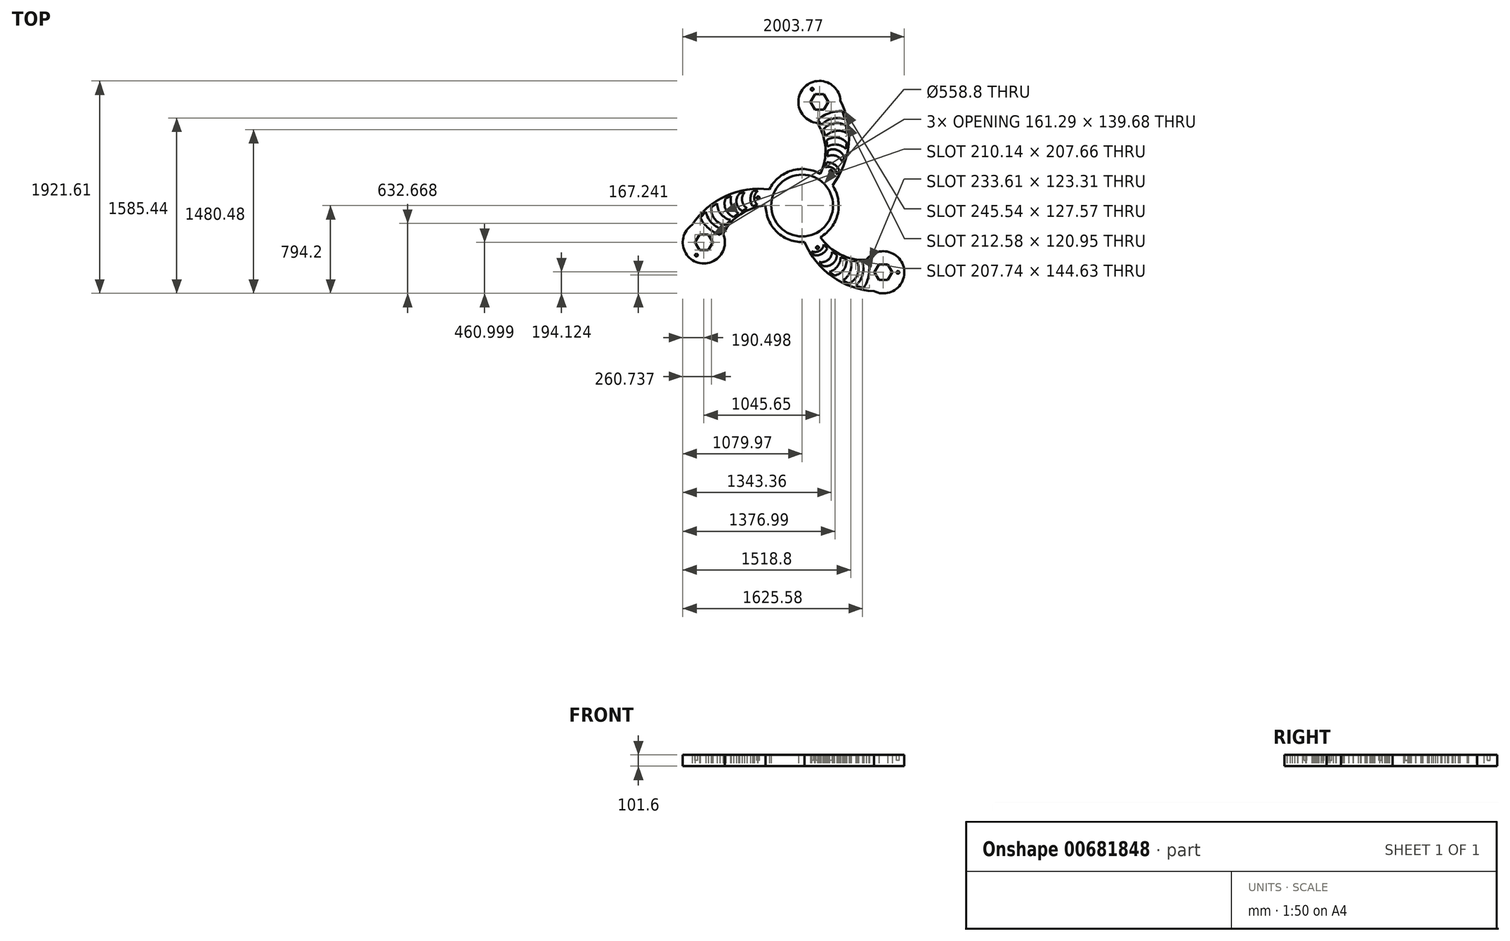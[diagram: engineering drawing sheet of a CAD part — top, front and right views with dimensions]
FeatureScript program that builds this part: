
annotation { "Feature Type Name" : "Feature", "Feature Type Description" : "" }
export const myFeature = defineFeature(function(context is Context, id is Id, definition is map)
    precondition{}
    {
        {
            var Q0;
            Q0=qCreatedBy(makeId("Top.planeOp"),FACE);
            var sketch = newSketch(context, id + "F0", { "sketchPlane" : qUnion([Q0])});
            skCircle(sketch, "E0", {"center": v(0, 0) * mm, "radius": 330.2 * mm});
            skArc(sketch, "E1", {"start": v(-295.98, 146.38) * mm, "mid": v(-691.32, 85.79) * mm, "end": v(-994.94, -174.56) * mm});
            skArc(sketch, "E2", {"start": v(-330.2, 0) * mm, "mid": v(-555.62, -78.09) * mm, "end": v(-715.84, -254.83) * mm});
            skArc(sketch, "E3", {"start": v(-818.87, -156.27) * mm, "mid": v(-998.12, -489.68) * mm, "end": v(-748.36, -205.22) * mm});
            skArc(sketch, "E4", {"start": v(-444.2, 130.87) * mm, "mid": v(-467.95, 63.66) * mm, "end": v(-447.52, -4.64) * mm});
            skLineSegment(sketch, "E5", {"start": v(-447.52, -4.64) * mm, "end": v(-403.07, 7.83) * mm});
            skLineSegment(sketch, "E6", {"start": v(-444.2, 130.87) * mm, "end": v(-399.74, 133.02) * mm});
            skArc(sketch, "E7", {"start": v(-399.74, 133.02) * mm, "mid": v(-432.98, 71.27) * mm, "end": v(-403.07, 7.83) * mm});
            skPoint(sketch, "E8.end.orphan", {"position": v(-453.15, 0) * mm});
            skLineSegment(sketch, "E9", {"start": v(-544.04, -48.42) * mm, "end": v(-498.32, -24.6) * mm});
            skLineSegment(sketch, "E10", {"start": v(-566.11, 110.29) * mm, "end": v(-520.4, 120.58) * mm});
            skArc(sketch, "E11", {"start": v(-520.4, 120.58) * mm, "mid": v(-542.84, 42.9) * mm, "end": v(-498.32, -24.6) * mm});
            skLineSegment(sketch, "E12", {"start": v(-620.12, -103.4) * mm, "end": v(-576.11, -68.97) * mm});
            skLineSegment(sketch, "E13", {"start": v(-693.63, 63.67) * mm, "end": v(-642.31, 85.79) * mm});
            skPoint(sketch, "E13.endSnap0", {"position": v(-691.32, 85.79) * mm});
            skArc(sketch, "E14", {"start": v(-693.63, 63.67) * mm, "mid": v(-690.53, -34.67) * mm, "end": v(-620.12, -103.4) * mm});
            skArc(sketch, "E15", {"start": v(-566.11, 110.29) * mm, "mid": v(-593.67, 25.57) * mm, "end": v(-544.04, -48.42) * mm});
            skArc(sketch, "E16", {"start": v(-642.31, 85.79) * mm, "mid": v(-634.72, -2.5) * mm, "end": v(-576.11, -68.97) * mm});
            skLineSegment(sketch, "E17", {"start": v(-821.71, -15.36) * mm, "end": v(-769.83, 21.24) * mm});
            skLineSegment(sketch, "E18", {"start": v(-689.25, -177.7) * mm, "end": v(-647.8, -129.6) * mm});
            skArc(sketch, "E19", {"start": v(-821.71, -15.36) * mm, "mid": v(-788.75, -123.68) * mm, "end": v(-689.25, -177.7) * mm});
            skArc(sketch, "E20", {"start": v(-769.83, 21.24) * mm, "mid": v(-735.26, -75.57) * mm, "end": v(-647.8, -129.6) * mm});
            skCircle(sketch, "E21.cCircle", {"center": v(-889.47, -333.2) * mm, "radius": 80.65 * mm, "construction": true});
            skLineSegment(sketch, "E21.0", {"start": v(-808.83, -333.2) * mm, "end": v(-849.15, -403.04) * mm});
            skLineSegment(sketch, "E21.1", {"start": v(-849.15, -403.04) * mm, "end": v(-929.8, -403.04) * mm});
            skLineSegment(sketch, "E21.2", {"start": v(-929.8, -403.04) * mm, "end": v(-970.12, -333.2) * mm});
            skLineSegment(sketch, "E21.3", {"start": v(-970.12, -333.2) * mm, "end": v(-929.8, -263.36) * mm});
            skLineSegment(sketch, "E21.4", {"start": v(-929.8, -263.36) * mm, "end": v(-849.15, -263.36) * mm});
            skLineSegment(sketch, "E21.5", {"start": v(-849.15, -263.36) * mm, "end": v(-808.83, -333.2) * mm});
            skLineSegment(sketch, "E22", {"start": v(-870.12, -56.46) * mm, "end": v(-923.06, -111.26) * mm});
            skLineSegment(sketch, "E23", {"start": v(-715.4, -215.8) * mm, "end": v(-743, -266.6) * mm});
            skArc(sketch, "E24", {"start": v(-870.12, -56.46) * mm, "mid": v(-816.29, -158.98) * mm, "end": v(-715.4, -215.8) * mm});
            skArc(sketch, "E25", {"start": v(-923.06, -111.26) * mm, "mid": v(-847.1, -205.24) * mm, "end": v(-743, -266.6) * mm});
            skArc(sketch, "E26.1.0", {"start": v(165.1, -285.96) * mm, "mid": v(345.43, -442.13) * mm, "end": v(578.6, -492.52) * mm});
            skArc(sketch, "E26.1.1", {"start": v(21.22, -329.52) * mm, "mid": v(271.37, -641.6) * mm, "end": v(648.64, -774.36) * mm});
            skArc(sketch, "E26.2.0", {"start": v(165.1, 285.96) * mm, "mid": v(210.18, 520.22) * mm, "end": v(137.23, 747.35) * mm});
            skArc(sketch, "E26.2.1", {"start": v(274.76, 183.14) * mm, "mid": v(419.96, 555.8) * mm, "end": v(346.3, 948.92) * mm});
            skLineSegment(sketch, "E27.1.0", {"start": v(813.94, -603.7) * mm, "end": v(773.62, -673.55) * mm});
            skLineSegment(sketch, "E27.1.1", {"start": v(692.97, -673.55) * mm, "end": v(652.65, -603.7) * mm});
            skLineSegment(sketch, "E27.1.2", {"start": v(773.62, -673.55) * mm, "end": v(692.97, -673.55) * mm});
            skLineSegment(sketch, "E27.2.0", {"start": v(115.85, 1006.75) * mm, "end": v(196.5, 1006.75) * mm});
            skLineSegment(sketch, "E27.2.1", {"start": v(236.82, 936.9) * mm, "end": v(196.5, 867.07) * mm});
            skLineSegment(sketch, "E27.2.2", {"start": v(196.5, 1006.75) * mm, "end": v(236.82, 936.9) * mm});
            skLineSegment(sketch, "E28.1.0", {"start": v(187.54, -545.4) * mm, "end": v(155.77, -510.96) * mm});
            skLineSegment(sketch, "E28.1.2", {"start": v(291.67, -632.53) * mm, "end": v(246.86, -599.15) * mm});
            skLineSegment(sketch, "E28.1.3", {"start": v(424.16, -703.94) * mm, "end": v(366.51, -677.31) * mm});
            skArc(sketch, "E28.1.4", {"start": v(544.77, -631.03) * mm, "mid": v(923.14, -619.56) * mm, "end": v(551.9, -545.49) * mm});
            skCircle(sketch, "E28.1.5", {"center": v(733.3, -603.7) * mm, "radius": 80.65 * mm, "construction": true});
            skLineSegment(sketch, "E28.1.6", {"start": v(399.62, -485.34) * mm, "end": v(347.8, -464.44) * mm});
            skArc(sketch, "E28.1.8", {"start": v(246.86, -599.15) * mm, "mid": v(319.53, -548.43) * mm, "end": v(347.8, -464.44) * mm});
            skLineSegment(sketch, "E28.1.10", {"start": v(483.96, -725.31) * mm, "end": v(557.89, -743.76) * mm});
            skArc(sketch, "E28.1.11", {"start": v(155.77, -510.96) * mm, "mid": v(234.26, -491.56) * mm, "end": v(270.46, -419.26) * mm});
            skLineSegment(sketch, "E28.1.12", {"start": v(108.76, -450.11) * mm, "end": v(84.67, -412.7) * mm});
            skArc(sketch, "E28.1.13", {"start": v(291.67, -632.53) * mm, "mid": v(375.3, -580.68) * mm, "end": v(399.62, -485.34) * mm});
            skArc(sketch, "E28.1.15", {"start": v(424.16, -703.94) * mm, "mid": v(501.48, -621.24) * mm, "end": v(498.52, -508.06) * mm});
            skArc(sketch, "E28.1.16", {"start": v(366.51, -677.31) * mm, "mid": v(433.08, -598.97) * mm, "end": v(436.13, -496.2) * mm});
            skLineSegment(sketch, "E28.1.17", {"start": v(227.78, -385.24) * mm, "end": v(194.75, -352.98) * mm});
            skArc(sketch, "E28.1.18", {"start": v(108.76, -450.11) * mm, "mid": v(178.85, -437.09) * mm, "end": v(227.78, -385.24) * mm});
            skArc(sketch, "E28.1.19", {"start": v(557.89, -743.76) * mm, "mid": v(601.29, -630.99) * mm, "end": v(602.38, -510.16) * mm});
            skLineSegment(sketch, "E28.1.20", {"start": v(773.62, -533.86) * mm, "end": v(813.94, -603.7) * mm});
            skLineSegment(sketch, "E28.1.21", {"start": v(498.52, -508.06) * mm, "end": v(436.13, -496.2) * mm});
            skArc(sketch, "E28.1.23", {"start": v(84.67, -412.7) * mm, "mid": v(154.77, -410.6) * mm, "end": v(194.75, -352.98) * mm});
            skLineSegment(sketch, "E28.1.24", {"start": v(313.95, -446.94) * mm, "end": v(270.46, -419.26) * mm});
            skArc(sketch, "E28.1.25", {"start": v(187.54, -545.4) * mm, "mid": v(274.7, -526.92) * mm, "end": v(313.95, -446.94) * mm});
            skLineSegment(sketch, "E28.1.26", {"start": v(544.6, -511.66) * mm, "end": v(602.38, -510.16) * mm});
            skLineSegment(sketch, "E28.1.27", {"start": v(652.65, -603.7) * mm, "end": v(692.97, -533.86) * mm});
            skLineSegment(sketch, "E28.1.28", {"start": v(692.97, -533.86) * mm, "end": v(773.62, -533.86) * mm});
            skArc(sketch, "E28.1.29", {"start": v(483.96, -725.31) * mm, "mid": v(545.82, -627.44) * mm, "end": v(544.6, -511.66) * mm});
            skLineSegment(sketch, "E28.2.0", {"start": v(378.57, 435.12) * mm, "end": v(364.62, 390.38) * mm});
            skLineSegment(sketch, "E28.2.2", {"start": v(401.95, 568.86) * mm, "end": v(395.45, 513.36) * mm});
            skLineSegment(sketch, "E28.2.3", {"start": v(397.55, 719.3) * mm, "end": v(403.31, 656.07) * mm});
            skArc(sketch, "E28.2.4", {"start": v(274.1, 787.3) * mm, "mid": v(74.98, 1109.24) * mm, "end": v(196.45, 750.71) * mm});
            skCircle(sketch, "E28.2.5", {"center": v(156.18, 936.9) * mm, "radius": 80.65 * mm, "construction": true});
            skLineSegment(sketch, "E28.2.6", {"start": v(220.5, 588.75) * mm, "end": v(228.32, 533.42) * mm});
            skArc(sketch, "E28.2.8", {"start": v(395.45, 513.36) * mm, "mid": v(315.2, 550.93) * mm, "end": v(228.32, 533.42) * mm});
            skLineSegment(sketch, "E28.2.10", {"start": v(386.16, 781.77) * mm, "end": v(365.17, 855.03) * mm});
            skArc(sketch, "E28.2.11", {"start": v(364.62, 390.38) * mm, "mid": v(308.58, 448.66) * mm, "end": v(227.86, 443.85) * mm});
            skLineSegment(sketch, "E28.2.12", {"start": v(335.43, 319.25) * mm, "end": v(315.07, 279.67) * mm});
            skArc(sketch, "E28.2.13", {"start": v(401.95, 568.86) * mm, "mid": v(315.23, 615.35) * mm, "end": v(220.5, 588.75) * mm});
            skArc(sketch, "E28.2.15", {"start": v(397.55, 719.3) * mm, "mid": v(287.27, 744.92) * mm, "end": v(190.73, 685.76) * mm});
            skArc(sketch, "E28.2.16", {"start": v(403.31, 656.07) * mm, "mid": v(302.18, 674.54) * mm, "end": v(211.66, 625.8) * mm});
            skLineSegment(sketch, "E28.2.17", {"start": v(219.74, 389.88) * mm, "end": v(208.32, 345.15) * mm});
            skArc(sketch, "E28.2.18", {"start": v(335.43, 319.25) * mm, "mid": v(289.1, 373.43) * mm, "end": v(219.74, 389.88) * mm});
            skArc(sketch, "E28.2.19", {"start": v(365.17, 855.03) * mm, "mid": v(245.8, 836.22) * mm, "end": v(140.62, 776.76) * mm});
            skLineSegment(sketch, "E28.2.20", {"start": v(75.53, 936.9) * mm, "end": v(115.85, 1006.75) * mm});
            skLineSegment(sketch, "E28.2.21", {"start": v(190.73, 685.76) * mm, "end": v(211.66, 625.8) * mm});
            skArc(sketch, "E28.2.23", {"start": v(315.07, 279.67) * mm, "mid": v(278.2, 339.34) * mm, "end": v(208.32, 345.15) * mm});
            skLineSegment(sketch, "E28.2.24", {"start": v(230.1, 495.36) * mm, "end": v(227.86, 443.85) * mm});
            skArc(sketch, "E28.2.25", {"start": v(378.57, 435.12) * mm, "mid": v(318.98, 501.35) * mm, "end": v(230.1, 495.36) * mm});
            skLineSegment(sketch, "E28.2.26", {"start": v(170.81, 727.46) * mm, "end": v(140.62, 776.76) * mm});
            skLineSegment(sketch, "E28.2.27", {"start": v(196.5, 867.07) * mm, "end": v(115.85, 867.07) * mm});
            skLineSegment(sketch, "E28.2.28", {"start": v(115.85, 867.07) * mm, "end": v(75.53, 936.9) * mm});
            skArc(sketch, "E28.2.29", {"start": v(386.16, 781.77) * mm, "mid": v(270.47, 786.42) * mm, "end": v(170.81, 727.46) * mm});
            skCircle(sketch, "E29", {"center": v(0, 0) * mm, "radius": 279.4 * mm});
            skSolve(sketch);
        }
        {
            var Q0;
            Q0=qSketchRegion(id+"F0",true);
            extrude(context, id + "F1", {"entities" : qUnion([Q0]), "depth" : 101.6 * mm, "offsetDistance" : 25.4 * mm});
        }
        {
            var Q0;
            Q0=makeQuery(id+"F1.opExtrude","CAP_FACE",FACE,{"disambiguationData":[OSD([sQuery(id+"F0.wireOp",EDGE,"E0"),sQuery(id+"F0.wireOp",EDGE,"E1"),sQuery(id+"F0.wireOp",EDGE,"E2"),sQuery(id+"F0.wireOp",EDGE,"E3"),sQuery(id+"F0.wireOp",EDGE,"E4"),sQuery(id+"F0.wireOp",EDGE,"E5"),sQuery(id+"F0.wireOp",EDGE,"E6"),sQuery(id+"F0.wireOp",EDGE,"E7"),sQuery(id+"F0.wireOp",EDGE,"E9"),sQuery(id+"F0.wireOp",EDGE,"E10"),sQuery(id+"F0.wireOp",EDGE,"E11"),sQuery(id+"F0.wireOp",EDGE,"E12"),sQuery(id+"F0.wireOp",EDGE,"E13"),sQuery(id+"F0.wireOp",EDGE,"E14"),sQuery(id+"F0.wireOp",EDGE,"E15"),sQuery(id+"F0.wireOp",EDGE,"E16"),sQuery(id+"F0.wireOp",EDGE,"E17"),sQuery(id+"F0.wireOp",EDGE,"E18"),sQuery(id+"F0.wireOp",EDGE,"E19"),sQuery(id+"F0.wireOp",EDGE,"E20"),sQuery(id+"F0.wireOp",EDGE,"E21.0"),sQuery(id+"F0.wireOp",EDGE,"E21.1"),sQuery(id+"F0.wireOp",EDGE,"E21.2"),sQuery(id+"F0.wireOp",EDGE,"E21.3"),sQuery(id+"F0.wireOp",EDGE,"E21.4"),sQuery(id+"F0.wireOp",EDGE,"E21.5"),sQuery(id+"F0.wireOp",EDGE,"E22"),sQuery(id+"F0.wireOp",EDGE,"E23"),sQuery(id+"F0.wireOp",EDGE,"E24"),sQuery(id+"F0.wireOp",EDGE,"E25"),sQuery(id+"F0.wireOp",EDGE,"E28.1.0"),sQuery(id+"F0.wireOp",EDGE,"E26.1.0"),sQuery(id+"F0.wireOp",EDGE,"E28.1.2"),sQuery(id+"F0.wireOp",EDGE,"E28.1.3"),sQuery(id+"F0.wireOp",EDGE,"E28.1.4"),sQuery(id+"F0.wireOp",EDGE,"E28.1.6"),sQuery(id+"F0.wireOp",EDGE,"E27.1.0"),sQuery(id+"F0.wireOp",EDGE,"E28.1.8"),sQuery(id+"F0.wireOp",EDGE,"E27.1.1"),sQuery(id+"F0.wireOp",EDGE,"E28.1.10"),sQuery(id+"F0.wireOp",EDGE,"E28.1.11"),sQuery(id+"F0.wireOp",EDGE,"E28.1.12"),sQuery(id+"F0.wireOp",EDGE,"E28.1.13"),sQuery(id+"F0.wireOp",EDGE,"E26.1.1"),sQuery(id+"F0.wireOp",EDGE,"E28.1.15"),sQuery(id+"F0.wireOp",EDGE,"E28.1.16"),sQuery(id+"F0.wireOp",EDGE,"E28.1.17"),sQuery(id+"F0.wireOp",EDGE,"E28.1.18"),sQuery(id+"F0.wireOp",EDGE,"E28.1.19"),sQuery(id+"F0.wireOp",EDGE,"E28.1.20"),sQuery(id+"F0.wireOp",EDGE,"E28.1.21"),sQuery(id+"F0.wireOp",EDGE,"E27.1.2"),sQuery(id+"F0.wireOp",EDGE,"E28.1.23"),sQuery(id+"F0.wireOp",EDGE,"E28.1.24"),sQuery(id+"F0.wireOp",EDGE,"E28.1.25"),sQuery(id+"F0.wireOp",EDGE,"E28.1.26"),sQuery(id+"F0.wireOp",EDGE,"E28.1.27"),sQuery(id+"F0.wireOp",EDGE,"E28.1.28"),sQuery(id+"F0.wireOp",EDGE,"E28.1.29"),sQuery(id+"F0.wireOp",EDGE,"E28.2.0"),sQuery(id+"F0.wireOp",EDGE,"E26.2.0"),sQuery(id+"F0.wireOp",EDGE,"E28.2.2"),sQuery(id+"F0.wireOp",EDGE,"E28.2.3"),sQuery(id+"F0.wireOp",EDGE,"E28.2.4"),sQuery(id+"F0.wireOp",EDGE,"E28.2.6"),sQuery(id+"F0.wireOp",EDGE,"E27.2.0"),sQuery(id+"F0.wireOp",EDGE,"E28.2.8"),sQuery(id+"F0.wireOp",EDGE,"E27.2.1"),sQuery(id+"F0.wireOp",EDGE,"E28.2.10"),sQuery(id+"F0.wireOp",EDGE,"E28.2.11"),sQuery(id+"F0.wireOp",EDGE,"E28.2.12"),sQuery(id+"F0.wireOp",EDGE,"E28.2.13"),sQuery(id+"F0.wireOp",EDGE,"E26.2.1"),sQuery(id+"F0.wireOp",EDGE,"E28.2.15"),sQuery(id+"F0.wireOp",EDGE,"E28.2.16"),sQuery(id+"F0.wireOp",EDGE,"E28.2.17"),sQuery(id+"F0.wireOp",EDGE,"E28.2.18"),sQuery(id+"F0.wireOp",EDGE,"E28.2.19"),sQuery(id+"F0.wireOp",EDGE,"E28.2.20"),sQuery(id+"F0.wireOp",EDGE,"E28.2.21"),sQuery(id+"F0.wireOp",EDGE,"E27.2.2"),sQuery(id+"F0.wireOp",EDGE,"E28.2.23"),sQuery(id+"F0.wireOp",EDGE,"E28.2.24"),sQuery(id+"F0.wireOp",EDGE,"E28.2.25"),sQuery(id+"F0.wireOp",EDGE,"E28.2.26"),sQuery(id+"F0.wireOp",EDGE,"E28.2.27"),sQuery(id+"F0.wireOp",EDGE,"E28.2.28"),sQuery(id+"F0.wireOp",EDGE,"E28.2.29"),sQuery(id+"F0.wireOp",EDGE,"E29")])],"isStart":false});
            var sketch = newSketch(context, id + "F2", { "sketchPlane" : qUnion([Q0])});
            skCircle(sketch, "E30", {"center": v(138.18, -380.01) * mm, "radius": 12.7 * mm});
            skCircle(sketch, "E31.1.0", {"center": v(260.01, 309.67) * mm, "radius": 12.7 * mm});
            skCircle(sketch, "E31.2.0", {"center": v(-398.2, 70.34) * mm, "radius": 12.7 * mm});
            skPoint(sketch, "E31.center", {"position": v(0, 0) * mm});
            skCircle(sketch, "E32", {"center": v(866.3, -604.3) * mm, "radius": 12.5 * mm});
            skCircle(sketch, "E33.1.0", {"center": v(90.18, 1052.38) * mm, "radius": 12.5 * mm});
            skCircle(sketch, "E33.2.0", {"center": v(-956.48, -448.09) * mm, "radius": 12.5 * mm});
            skSolve(sketch);
        }
        {
            var Q0;
            Q0 = qSketchRegion(id + "F2", true);
            extrude(context, id + "F3", {"entities" : qUnion([Q0]), "operationType" : NewBodyOperationType.REMOVE, "oppositeDirection" : true, "depth" : 50.8 * mm, "offsetDistance" : 25 * mm});
        }
    });
